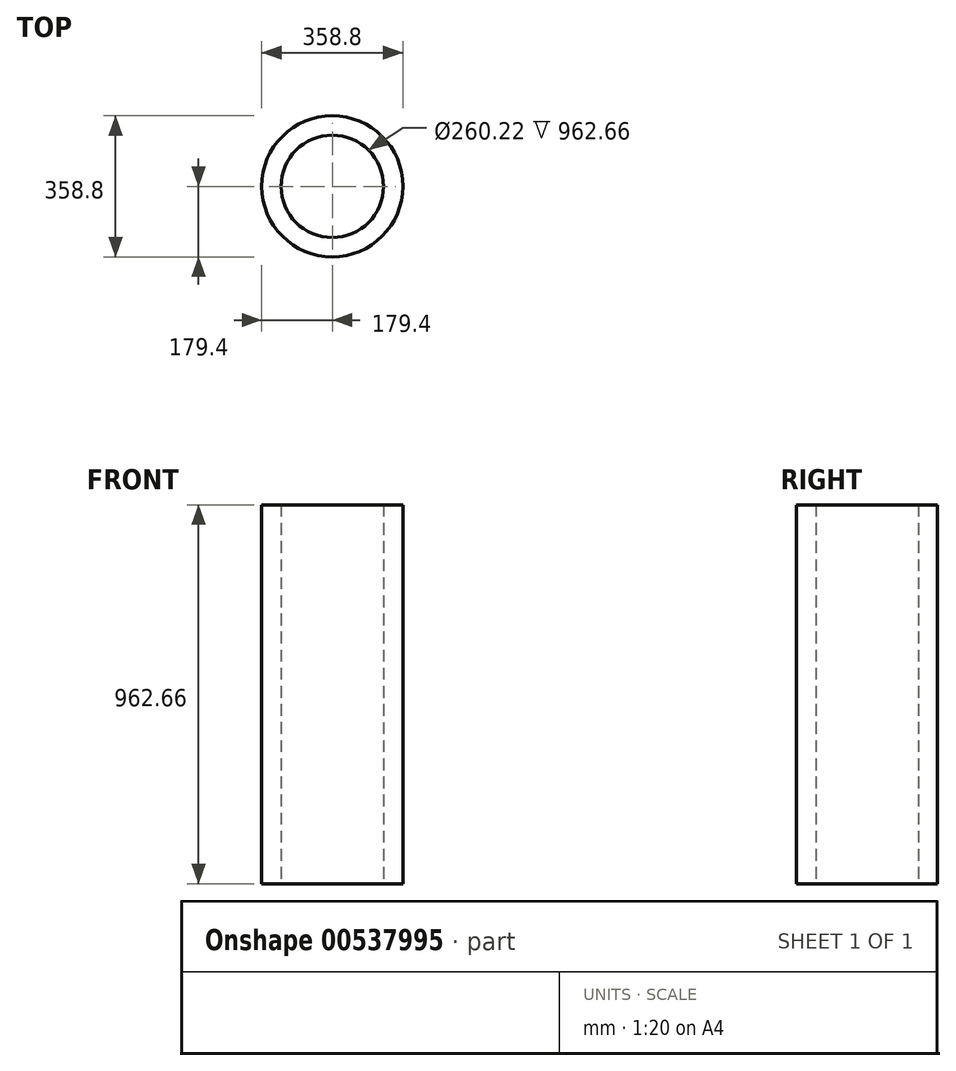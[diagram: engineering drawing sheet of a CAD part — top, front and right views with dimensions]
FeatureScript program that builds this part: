
annotation { "Feature Type Name" : "Feature", "Feature Type Description" : "" }
export const myFeature = defineFeature(function(context is Context, id is Id, definition is map)
    precondition{}
    {
        {
            var Q0;
            Q0=qCreatedBy(makeId("Top.planeOp"),FACE);
            var sketch = newSketch(context, id + "F0", { "sketchPlane" : qUnion([Q0])});
            skCircle(sketch, "E0", {"center": v(0, 0) * mm, "radius": 179.4 * mm});
            skCircle(sketch, "E1", {"center": v(0, 0) * mm, "radius": 130.11 * mm});
            skSolve(sketch);
        }
        {
            var Q0;
            Q0=makeQuery(id+"F0.imprint","IMPRINT",FACE,{"disambiguationData":[TD([[makeQuery(id+"F0.imprint","IMPRINT",EDGE,{"derivedFrom":sQuery(id+"F0.wireOp",EDGE,"E0")}),1.0]])]});
            extrude(context, id + "F1", {"entities" : qUnion([Q0]), "depth" : 962.66 * mm, "offsetDistance" : 25.4 * mm});
        }
    });
